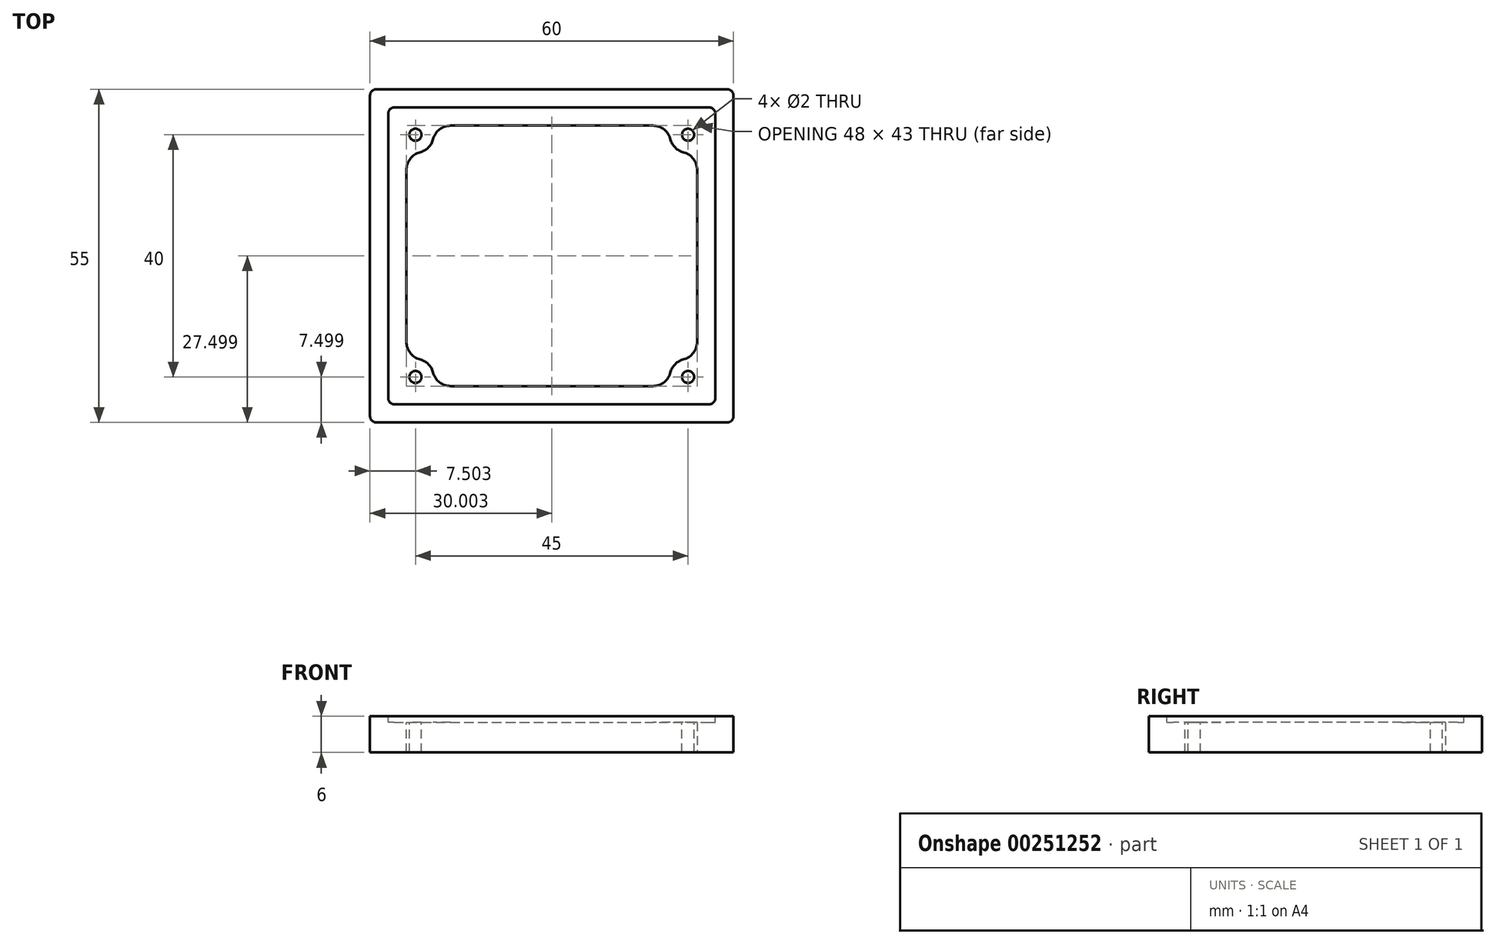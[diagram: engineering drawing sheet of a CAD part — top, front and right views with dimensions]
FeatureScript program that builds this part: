
annotation { "Feature Type Name" : "Feature", "Feature Type Description" : "" }
export const myFeature = defineFeature(function(context is Context, id is Id, definition is map)
    precondition{}
    {
        {
            var Q0;
            Q0=qCreatedBy(makeId("Top.planeOp"),FACE);
            var sketch = newSketch(context, id + "F0", { "sketchPlane" : qUnion([Q0])});
            skLineSegment(sketch, "E0.bottom", {"start": v(-17.99, 39.67) * mm, "end": v(42.01, 39.67) * mm});
            skLineSegment(sketch, "E0.top", {"start": v(-17.99, -15.33) * mm, "end": v(42.01, -15.33) * mm});
            skLineSegment(sketch, "E0.left", {"start": v(-17.99, 39.67) * mm, "end": v(-17.99, -15.33) * mm});
            skLineSegment(sketch, "E0.right", {"start": v(42.01, 39.67) * mm, "end": v(42.01, -15.33) * mm});
            skSolve(sketch);
        }
        {
            var Q0;
            Q0=makeQuery(id+"F0.imprint","IMPRINT",FACE,{"disambiguationData":[TD([[makeQuery(id+"F0.imprint","IMPRINT",EDGE,{"derivedFrom":sQuery(id+"F0.wireOp",EDGE,"E0.bottom")}),-1.0]])]});
            extrude(context, id + "F1", {"entities" : qUnion([Q0]), "depth" : 6 * mm});
        }
        {
            var Q0;
            Q0=makeQuery(id+"F1.opExtrude","CAP_FACE",FACE,{"disambiguationData":[OSD([sQuery(id+"F0.wireOp",EDGE,"E0.bottom"),sQuery(id+"F0.wireOp",EDGE,"E0.top"),sQuery(id+"F0.wireOp",EDGE,"E0.left"),sQuery(id+"F0.wireOp",EDGE,"E0.right")])],"isStart":false});
            var sketch = newSketch(context, id + "F2", { "sketchPlane" : qUnion([Q0])});
            skLineSegment(sketch, "E1.bottom", {"start": v(-17.99, 39.67) * mm, "end": v(-14.99, 39.67) * mm});
            skLineSegment(sketch, "E1.top", {"start": v(-17.99, 36.67) * mm, "end": v(-14.99, 36.67) * mm});
            skLineSegment(sketch, "E1.left", {"start": v(-17.99, 39.67) * mm, "end": v(-17.99, 36.67) * mm});
            skLineSegment(sketch, "E1.right", {"start": v(-14.99, 39.67) * mm, "end": v(-14.99, 36.67) * mm});
            skLineSegment(sketch, "E2.bottom", {"start": v(42.01, -15.33) * mm, "end": v(39.01, -15.33) * mm});
            skLineSegment(sketch, "E2.top", {"start": v(42.01, -12.33) * mm, "end": v(39.01, -12.33) * mm});
            skLineSegment(sketch, "E2.left", {"start": v(42.01, -15.33) * mm, "end": v(42.01, -12.33) * mm});
            skLineSegment(sketch, "E2.right", {"start": v(39.01, -15.33) * mm, "end": v(39.01, -12.33) * mm});
            skLineSegment(sketch, "E3.bottom", {"start": v(-14.99, 36.67) * mm, "end": v(39.01, 36.67) * mm});
            skLineSegment(sketch, "E3.top", {"start": v(-14.99, -12.33) * mm, "end": v(39.01, -12.33) * mm});
            skLineSegment(sketch, "E3.left", {"start": v(-14.99, 36.67) * mm, "end": v(-14.99, -12.33) * mm});
            skLineSegment(sketch, "E3.right", {"start": v(39.01, 36.67) * mm, "end": v(39.01, -12.33) * mm});
            skSolve(sketch);
        }
        {
            var Q0;
            Q0=makeQuery(id+"F2.imprint","IMPRINT",FACE,{"disambiguationData":[TD([[makeQuery(id+"F2.imprint","IMPRINT",EDGE,{"derivedFrom":sQuery(id+"F2.wireOp",EDGE,"E3.bottom")}),-1.0]])]});
            extrude(context, id + "F3", {"entities" : qUnion([Q0]), "operationType" : NewBodyOperationType.REMOVE, "oppositeDirection" : true, "depth" : 1 * mm});
        }
        {
            var Q0;
            Q0=makeQuery(id+"F3.boolean.opBoolean","COPY",FACE,{"derivedFrom":makeQuery(id+"F3.opExtrude","CAP_FACE",FACE,{"disambiguationData":[OSD([sQuery(id+"F2.wireOp",EDGE,"E3.bottom"),sQuery(id+"F2.wireOp",EDGE,"E3.top"),sQuery(id+"F2.wireOp",EDGE,"E3.left"),sQuery(id+"F2.wireOp",EDGE,"E3.right")])],"isStart":false})});
            var sketch = newSketch(context, id + "F4", { "sketchPlane" : qUnion([Q0])});
            skLineSegment(sketch, "E4.bottom", {"start": v(-14.99, 36.67) * mm, "end": v(-11.99, 36.67) * mm});
            skLineSegment(sketch, "E4.top", {"start": v(-14.99, 33.67) * mm, "end": v(-11.99, 33.67) * mm});
            skLineSegment(sketch, "E4.left", {"start": v(-14.99, 36.67) * mm, "end": v(-14.99, 33.67) * mm});
            skLineSegment(sketch, "E4.right", {"start": v(-11.99, 36.67) * mm, "end": v(-11.99, 33.67) * mm});
            skLineSegment(sketch, "E5.bottom", {"start": v(39.01, -12.33) * mm, "end": v(36.01, -12.33) * mm});
            skLineSegment(sketch, "E5.top", {"start": v(39.01, -9.33) * mm, "end": v(36.01, -9.33) * mm});
            skLineSegment(sketch, "E5.left", {"start": v(39.01, -12.33) * mm, "end": v(39.01, -9.33) * mm});
            skLineSegment(sketch, "E5.right", {"start": v(36.01, -12.33) * mm, "end": v(36.01, -9.33) * mm});
            skLineSegment(sketch, "E6.bottom", {"start": v(-11.99, 33.67) * mm, "end": v(36.01, 33.67) * mm});
            skLineSegment(sketch, "E6.top", {"start": v(-11.99, -9.33) * mm, "end": v(36.01, -9.33) * mm});
            skLineSegment(sketch, "E6.left", {"start": v(-11.99, 33.67) * mm, "end": v(-11.99, -9.33) * mm});
            skLineSegment(sketch, "E6.right", {"start": v(36.01, 33.67) * mm, "end": v(36.01, -9.33) * mm});
            skSolve(sketch);
        }
        {
            var Q0;
            Q0=makeQuery(id+"F4.imprint","IMPRINT",FACE,{"disambiguationData":[TD([[makeQuery(id+"F4.imprint","IMPRINT",EDGE,{"derivedFrom":sQuery(id+"F4.wireOp",EDGE,"E6.bottom")}),-1.0]])]});
            extrude(context, id + "F5", {"entities" : qUnion([Q0]), "operationType" : NewBodyOperationType.REMOVE, "oppositeDirection" : true, "depth" : 25 * mm});
        }
        {
            var Q0;
            Q0=makeQuery(id+"F1.opExtrude","CAP_FACE",FACE,{"disambiguationData":[OSD([sQuery(id+"F0.wireOp",EDGE,"E0.bottom"),sQuery(id+"F0.wireOp",EDGE,"E0.top"),sQuery(id+"F0.wireOp",EDGE,"E0.left"),sQuery(id+"F0.wireOp",EDGE,"E0.right")])],"isStart":false});
            var sketch = newSketch(context, id + "F6", { "sketchPlane" : qUnion([Q0])});
            skLineSegment(sketch, "E7.bottom", {"start": v(-17.99, 39.67) * mm, "end": v(-10.49, 39.67) * mm});
            skLineSegment(sketch, "E7.left", {"start": v(-17.99, 39.67) * mm, "end": v(-17.99, 32.17) * mm});
            skLineSegment(sketch, "E8.bottom", {"start": v(42.01, -15.33) * mm, "end": v(34.51, -15.33) * mm});
            skLineSegment(sketch, "E8.left", {"start": v(42.01, -15.33) * mm, "end": v(42.01, -7.83) * mm});
            skLineSegment(sketch, "E9.bottom", {"start": v(-17.99, -15.33) * mm, "end": v(-10.49, -15.33) * mm});
            skLineSegment(sketch, "E9.left", {"start": v(-17.99, -15.33) * mm, "end": v(-17.99, -7.83) * mm});
            skLineSegment(sketch, "E10.bottom", {"start": v(42.01, 39.67) * mm, "end": v(34.51, 39.67) * mm});
            skLineSegment(sketch, "E10.left", {"start": v(42.01, 39.67) * mm, "end": v(42.01, 32.17) * mm});
            skCircle(sketch, "E11", {"center": v(-10.49, 32.17) * mm, "radius": 3 * mm});
            skCircle(sketch, "E12", {"center": v(-10.49, -7.83) * mm, "radius": 3 * mm});
            skCircle(sketch, "E13", {"center": v(34.51, -7.83) * mm, "radius": 3 * mm});
            skCircle(sketch, "E14", {"center": v(34.51, 32.17) * mm, "radius": 3 * mm});
            skSolve(sketch);
        }
        {
            var Q0;
            Q0=makeQuery(id+"F6.imprint","IMPRINT",FACE,{"disambiguationData":[TD([[makeQuery(id+"F6.imprint","IMPRINT",EDGE,{"derivedFrom":sQuery(id+"F6.wireOp",EDGE,"E11")}),1.0]])]});
            var Q1;
            Q1=makeQuery(id+"F6.imprint","IMPRINT",FACE,{"disambiguationData":[TD([[makeQuery(id+"F6.imprint","IMPRINT",EDGE,{"derivedFrom":sQuery(id+"F6.wireOp",EDGE,"E14")}),1.0]])]});
            var Q2;
            Q2=makeQuery(id+"F6.imprint","IMPRINT",FACE,{"disambiguationData":[TD([[makeQuery(id+"F6.imprint","IMPRINT",EDGE,{"derivedFrom":sQuery(id+"F6.wireOp",EDGE,"E13")}),1.0]])]});
            var Q3;
            Q3=makeQuery(id+"F6.imprint","IMPRINT",FACE,{"disambiguationData":[TD([[makeQuery(id+"F6.imprint","IMPRINT",EDGE,{"derivedFrom":sQuery(id+"F6.wireOp",EDGE,"E12")}),1.0]])]});
            var Q4;
            Q4=makeQuery(id+"F1.opExtrude","CAP_FACE",FACE,{"disambiguationData":[OSD([sQuery(id+"F0.wireOp",EDGE,"E0.bottom"),sQuery(id+"F0.wireOp",EDGE,"E0.top"),sQuery(id+"F0.wireOp",EDGE,"E0.left"),sQuery(id+"F0.wireOp",EDGE,"E0.right")])],"isStart":true});
            extrude(context, id + "F7", {"entities" : qUnion([Q0, Q1, Q2, Q3]), "operationType" : NewBodyOperationType.ADD, "endBound" : BoundingType.UP_TO_SURFACE, "oppositeDirection" : true, "endBoundEntityFace" : qUnion([Q4]), "depth" : 25 * mm});
        }
        {
            var Q0;
            Q0=makeQuery(id+"F3.boolean.opBoolean","COPY",FACE,{"derivedFrom":makeQuery(id+"F3.opExtrude","SWEPT_FACE",FACE,{"disambiguationData":[OSD([sQuery(id+"F2.wireOp",EDGE,"E3.right")])]})});
            var Q1;
            Q1=makeQuery(id+"F3.boolean.opBoolean","COPY",FACE,{"derivedFrom":makeQuery(id+"F3.opExtrude","SWEPT_FACE",FACE,{"disambiguationData":[OSD([sQuery(id+"F2.wireOp",EDGE,"E3.left")])]})});
            extrude(context, id + "F8", {"entities" : qUnion([Q0]), "operationType" : NewBodyOperationType.REMOVE, "endBound" : BoundingType.UP_TO_SURFACE, "endBoundEntityFace" : qUnion([Q1]), "depth" : 25 * mm});
        }
        {
            var Q0;
            Q0=makeQuery(id+"F6.imprint","IMPRINT",FACE,{"disambiguationData":[TD([[makeQuery(id+"F6.imprint","IMPRINT",EDGE,{"derivedFrom":sQuery(id+"F6.wireOp",EDGE,"E11")}),-1.0]])]});
            var sketch = newSketch(context, id + "F9", { "sketchPlane" : qUnion([Q0])});
            skCircle(sketch, "E15", {"center": v(-10.49, 32.17) * mm, "radius": 1 * mm});
            skCircle(sketch, "E16", {"center": v(34.51, 32.17) * mm, "radius": 1 * mm});
            skCircle(sketch, "E17", {"center": v(-10.49, -7.83) * mm, "radius": 1 * mm});
            skCircle(sketch, "E18", {"center": v(34.51, -7.83) * mm, "radius": 1 * mm});
            skSolve(sketch);
        }
        {
            var Q0;
            Q0=makeQuery(id+"F9.imprint","IMPRINT",FACE,{"disambiguationData":[TD([[makeQuery(id+"F9.imprint","IMPRINT",EDGE,{"derivedFrom":sQuery(id+"F9.wireOp",EDGE,"E17")}),1.0]])]});
            var Q1;
            Q1=makeQuery(id+"F9.imprint","IMPRINT",FACE,{"disambiguationData":[TD([[makeQuery(id+"F9.imprint","IMPRINT",EDGE,{"derivedFrom":sQuery(id+"F9.wireOp",EDGE,"E18")}),1.0]])]});
            var Q2;
            Q2=makeQuery(id+"F9.imprint","IMPRINT",FACE,{"disambiguationData":[TD([[makeQuery(id+"F9.imprint","IMPRINT",EDGE,{"derivedFrom":sQuery(id+"F9.wireOp",EDGE,"E16")}),1.0]])]});
            var Q3;
            Q3=makeQuery(id+"F9.imprint","IMPRINT",FACE,{"disambiguationData":[TD([[makeQuery(id+"F9.imprint","IMPRINT",EDGE,{"derivedFrom":sQuery(id+"F9.wireOp",EDGE,"E15")}),1.0]])]});
            var Q4;
            Q4=sQuery(id+"F9.wireOp",EDGE,"E17");
            extrude(context, id + "F10", {"entities" : qUnion([Q0, Q1, Q2, Q3]), "operationType" : NewBodyOperationType.REMOVE, "surfaceEntities" : qUnion([Q4]), "oppositeDirection" : true, "depth" : 25 * mm});
        }
        {
            var Q0;
            Q0=makeQuery(id+"F7.boolean.opBoolean","INTERSECT",EDGE,{"derivedFrom":[makeQuery(id+"F5.boolean.opBoolean","COPY",FACE,{"derivedFrom":makeQuery(id+"F5.opExtrude","SWEPT_FACE",FACE,{"disambiguationData":[OSD([sQuery(id+"F4.wireOp",EDGE,"E6.bottom")])]})}),makeQuery(id+"F7.opExtrude","SWEPT_FACE",FACE,{"disambiguationData":[OSD([sQuery(id+"F6.wireOp",EDGE,"E11")])]})]});
            var Q1;
            Q1=makeQuery(id+"F7.boolean.opBoolean","INTERSECT",EDGE,{"derivedFrom":[makeQuery(id+"F5.boolean.opBoolean","COPY",FACE,{"derivedFrom":makeQuery(id+"F5.opExtrude","SWEPT_FACE",FACE,{"disambiguationData":[OSD([sQuery(id+"F4.wireOp",EDGE,"E6.left")])]})}),makeQuery(id+"F7.opExtrude","SWEPT_FACE",FACE,{"disambiguationData":[OSD([sQuery(id+"F6.wireOp",EDGE,"E11")])]})]});
            var Q2;
            Q2=makeQuery(id+"F7.boolean.opBoolean","INTERSECT",EDGE,{"derivedFrom":[makeQuery(id+"F5.boolean.opBoolean","COPY",FACE,{"derivedFrom":makeQuery(id+"F5.opExtrude","SWEPT_FACE",FACE,{"disambiguationData":[OSD([sQuery(id+"F4.wireOp",EDGE,"E6.right")])]})}),makeQuery(id+"F7.opExtrude","SWEPT_FACE",FACE,{"disambiguationData":[OSD([sQuery(id+"F6.wireOp",EDGE,"E14")])]})]});
            var Q3;
            Q3=makeQuery(id+"F7.boolean.opBoolean","INTERSECT",EDGE,{"derivedFrom":[makeQuery(id+"F5.boolean.opBoolean","COPY",FACE,{"derivedFrom":makeQuery(id+"F5.opExtrude","SWEPT_FACE",FACE,{"disambiguationData":[OSD([sQuery(id+"F4.wireOp",EDGE,"E6.bottom")])]})}),makeQuery(id+"F7.opExtrude","SWEPT_FACE",FACE,{"disambiguationData":[OSD([sQuery(id+"F6.wireOp",EDGE,"E14")])]})]});
            var Q4;
            Q4=makeQuery(id+"F7.boolean.opBoolean","INTERSECT",EDGE,{"derivedFrom":[makeQuery(id+"F5.boolean.opBoolean","COPY",FACE,{"derivedFrom":makeQuery(id+"F5.opExtrude","SWEPT_FACE",FACE,{"disambiguationData":[OSD([sQuery(id+"F4.wireOp",EDGE,"E6.right")])]})}),makeQuery(id+"F7.opExtrude","SWEPT_FACE",FACE,{"disambiguationData":[OSD([sQuery(id+"F6.wireOp",EDGE,"E13")])]})]});
            var Q5;
            Q5=makeQuery(id+"F7.boolean.opBoolean","INTERSECT",EDGE,{"derivedFrom":[makeQuery(id+"F5.boolean.opBoolean","COPY",FACE,{"derivedFrom":makeQuery(id+"F5.opExtrude","SWEPT_FACE",FACE,{"disambiguationData":[OSD([sQuery(id+"F4.wireOp",EDGE,"E6.top")])]})}),makeQuery(id+"F7.opExtrude","SWEPT_FACE",FACE,{"disambiguationData":[OSD([sQuery(id+"F6.wireOp",EDGE,"E13")])]})]});
            var Q6;
            Q6=makeQuery(id+"F7.boolean.opBoolean","INTERSECT",EDGE,{"derivedFrom":[makeQuery(id+"F5.boolean.opBoolean","COPY",FACE,{"derivedFrom":makeQuery(id+"F5.opExtrude","SWEPT_FACE",FACE,{"disambiguationData":[OSD([sQuery(id+"F4.wireOp",EDGE,"E6.left")])]})}),makeQuery(id+"F7.opExtrude","SWEPT_FACE",FACE,{"disambiguationData":[OSD([sQuery(id+"F6.wireOp",EDGE,"E12")])]})]});
            var Q7;
            Q7=makeQuery(id+"F7.boolean.opBoolean","INTERSECT",EDGE,{"derivedFrom":[makeQuery(id+"F5.boolean.opBoolean","COPY",FACE,{"derivedFrom":makeQuery(id+"F5.opExtrude","SWEPT_FACE",FACE,{"disambiguationData":[OSD([sQuery(id+"F4.wireOp",EDGE,"E6.top")])]})}),makeQuery(id+"F7.opExtrude","SWEPT_FACE",FACE,{"disambiguationData":[OSD([sQuery(id+"F6.wireOp",EDGE,"E12")])]})]});
            fillet(context, id + "F11", {"entities" : qUnion([Q0, Q1, Q2, Q3, Q4, Q5, Q6, Q7]), "radius" : 3 * mm, "tangentPropagation" : true, "allowEdgeOverflow" : false});
        }
        {
            var Q0;
            Q0=makeQuery(id+"F1.opExtrude","SWEPT_EDGE",EDGE,{"disambiguationData":[OSD([sQuery(id+"F0.wireOp",EDGE,"E0.top"),sQuery(id+"F0.wireOp",EDGE,"E0.left")])]});
            var Q1;
            Q1=makeQuery(id+"F1.opExtrude","SWEPT_EDGE",EDGE,{"disambiguationData":[OSD([sQuery(id+"F0.wireOp",EDGE,"E0.bottom"),sQuery(id+"F0.wireOp",EDGE,"E0.left")])]});
            var Q2;
            Q2=makeQuery(id+"F1.opExtrude","SWEPT_EDGE",EDGE,{"disambiguationData":[OSD([sQuery(id+"F0.wireOp",EDGE,"E0.bottom"),sQuery(id+"F0.wireOp",EDGE,"E0.right")])]});
            var Q3;
            Q3=makeQuery(id+"F1.opExtrude","SWEPT_EDGE",EDGE,{"disambiguationData":[OSD([sQuery(id+"F0.wireOp",EDGE,"E0.top"),sQuery(id+"F0.wireOp",EDGE,"E0.right")])]});
            var Q4;
            Q4=makeQuery(id+"F3.boolean.opBoolean","COPY",EDGE,{"derivedFrom":makeQuery(id+"F3.opExtrude","SWEPT_EDGE",EDGE,{"disambiguationData":[OSD([sQuery(id+"F2.wireOp",EDGE,"E3.bottom"),sQuery(id+"F2.wireOp",EDGE,"E3.right")])]})});
            var Q5;
            Q5=makeQuery(id+"F3.boolean.opBoolean","COPY",EDGE,{"derivedFrom":makeQuery(id+"F3.opExtrude","SWEPT_EDGE",EDGE,{"disambiguationData":[OSD([sQuery(id+"F2.wireOp",EDGE,"E1.top"),sQuery(id+"F2.wireOp",EDGE,"E1.right"),sQuery(id+"F2.wireOp",EDGE,"E3.bottom"),sQuery(id+"F2.wireOp",EDGE,"E3.left")])]})});
            var Q6;
            Q6=makeQuery(id+"F3.boolean.opBoolean","COPY",EDGE,{"derivedFrom":makeQuery(id+"F3.opExtrude","SWEPT_EDGE",EDGE,{"disambiguationData":[OSD([sQuery(id+"F2.wireOp",EDGE,"E3.top"),sQuery(id+"F2.wireOp",EDGE,"E3.left")])]})});
            var Q7;
            Q7=makeQuery(id+"F3.boolean.opBoolean","COPY",EDGE,{"derivedFrom":makeQuery(id+"F3.opExtrude","SWEPT_EDGE",EDGE,{"disambiguationData":[OSD([sQuery(id+"F2.wireOp",EDGE,"E2.top"),sQuery(id+"F2.wireOp",EDGE,"E2.right"),sQuery(id+"F2.wireOp",EDGE,"E3.top"),sQuery(id+"F2.wireOp",EDGE,"E3.right")])]})});
            fillet(context, id + "F12", {"entities" : qUnion([Q0, Q1, Q2, Q3, Q4, Q5, Q6, Q7]), "radius" : 1 * mm, "tangentPropagation" : true, "allowEdgeOverflow" : false});
        }
    });
